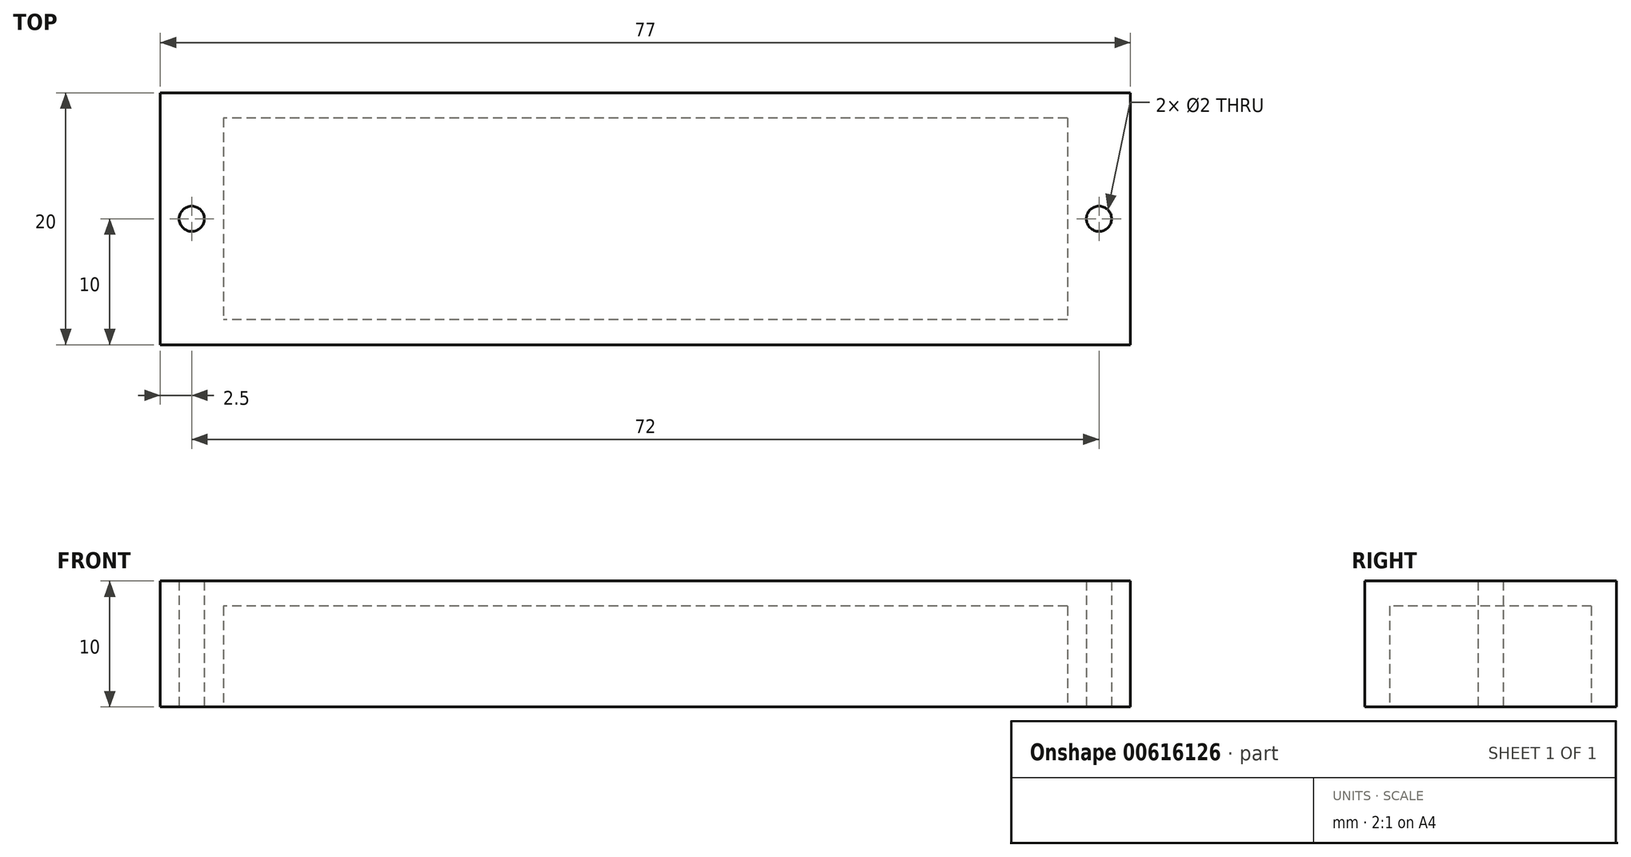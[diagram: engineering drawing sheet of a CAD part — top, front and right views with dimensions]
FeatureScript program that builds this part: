
annotation { "Feature Type Name" : "Feature", "Feature Type Description" : "" }
export const myFeature = defineFeature(function(context is Context, id is Id, definition is map)
    precondition{}
    {
        {
            var Q0;
            Q0=qCreatedBy(makeId("Top.planeOp"),FACE);
            var sketch = newSketch(context, id + "F0", { "sketchPlane" : qUnion([Q0])});
            skLineSegment(sketch, "E0.bottom", {"start": v(38.5, 10) * mm, "end": v(-38.5, 10) * mm});
            skLineSegment(sketch, "E0.top", {"start": v(38.5, -10) * mm, "end": v(-38.5, -10) * mm});
            skLineSegment(sketch, "E0.left", {"start": v(38.5, 10) * mm, "end": v(38.5, -10) * mm});
            skLineSegment(sketch, "E0.right", {"start": v(-38.5, 10) * mm, "end": v(-38.5, -10) * mm});
            skPoint(sketch, "E0.middle", {"position": v(0, 0) * mm});
            skPoint(sketch, "E1.left.start.orphan", {"position": v(33.5, 8) * mm});
            skPoint(sketch, "E1.top.start.orphan", {"position": v(33.5, -8) * mm});
            skPoint(sketch, "E1.right.end.orphan", {"position": v(-33.5, -8) * mm});
            skPoint(sketch, "E1.right.start.orphan", {"position": v(-33.5, 8) * mm});
            skSolve(sketch);
        }
        {
            var Q0;
            Q0 = qSketchRegion(id + "F0", true);
            extrude(context, id + "F1", {"entities" : qUnion([Q0]), "depth" : 10 * mm, "offsetDistance" : 25 * mm});
        }
        {
            var Q0;
            Q0=makeQuery(id+"F1.opExtrude","CAP_FACE",FACE,{"disambiguationData":[OSD([sQuery(id+"F0.wireOp",EDGE,"E0.bottom"),sQuery(id+"F0.wireOp",EDGE,"E0.top"),sQuery(id+"F0.wireOp",EDGE,"E0.left"),sQuery(id+"F0.wireOp",EDGE,"E0.right")])],"isStart":false});
            var sketch = newSketch(context, id + "F2", { "sketchPlane" : qUnion([Q0])});
            skLineSegment(sketch, "E2.bottom", {"start": v(33.5, 8) * mm, "end": v(-33.5, 8) * mm});
            skLineSegment(sketch, "E2.top", {"start": v(33.5, -8) * mm, "end": v(-33.5, -8) * mm});
            skLineSegment(sketch, "E2.left", {"start": v(33.5, 8) * mm, "end": v(33.5, -8) * mm});
            skLineSegment(sketch, "E2.right", {"start": v(-33.5, 8) * mm, "end": v(-33.5, -8) * mm});
            skPoint(sketch, "E2.middle", {"position": v(0, 0) * mm});
            skSolve(sketch);
        }
        {
            var Q0;
            Q0 = qSketchRegion(id + "F2", true);
            extrude(context, id + "F3", {"entities" : qUnion([Q0]), "operationType" : NewBodyOperationType.REMOVE, "oppositeDirection" : true, "depth" : 8 * mm, "offsetDistance" : 25 * mm});
        }
        {
            var Q0;
            Q0=qCreatedBy(makeId("Top.planeOp"),FACE);
            cPlane(context, id + "F4", {"entities" : qUnion([Q0]), "cplaneType" : CPlaneType.OFFSET, "offset" : 25 * mm, "width" : 150 * mm, "height" : 150 * mm});
        }
        {
            var Q0;
            Q0=makeQuery(id+"F1.opExtrude","SWEPT_BODY",BODY,{"disambiguationData":[OSD([sQuery(id+"F0.wireOp",EDGE,"E0.bottom"),sQuery(id+"F0.wireOp",EDGE,"E0.top"),sQuery(id+"F0.wireOp",EDGE,"E0.left"),sQuery(id+"F0.wireOp",EDGE,"E0.right")])]});
            var Q1;
            Q1=qCreatedBy(id+"F4.planeOp",FACE);
            mirror(context, id + "F5", {"entities" : qUnion([Q0]), "mirrorPlane" : qUnion([Q1])});
        }
        {
            var Q0;
            Q0=makeQuery(id+"F1.opExtrude","SWEPT_BODY",BODY,{"disambiguationData":[OSD([sQuery(id+"F0.wireOp",EDGE,"E0.bottom"),sQuery(id+"F0.wireOp",EDGE,"E0.top"),sQuery(id+"F0.wireOp",EDGE,"E0.left"),sQuery(id+"F0.wireOp",EDGE,"E0.right")])]});
            deleteBodies(context, id + "F6", {"entities" : qUnion([Q0])});
        }
        {
            var Q0;
            Q0=makeQuery(id+"F5.opPattern","COPY",FACE,{"derivedFrom":makeQuery(id+"F1.opExtrude","CAP_FACE",FACE,{"disambiguationData":[OSD([sQuery(id+"F0.wireOp",EDGE,"E0.bottom"),sQuery(id+"F0.wireOp",EDGE,"E0.top"),sQuery(id+"F0.wireOp",EDGE,"E0.left"),sQuery(id+"F0.wireOp",EDGE,"E0.right")])],"isStart":false}),"instanceName":"1"});
            var sketch = newSketch(context, id + "F7", { "sketchPlane" : qUnion([Q0])});
            skPoint(sketch, "E3", {"position": v(36, 0) * mm});
            skPoint(sketch, "E4", {"position": v(-36, 0) * mm});
            skCircle(sketch, "E5", {"center": v(36, 0) * mm, "radius": 1 * mm});
            skCircle(sketch, "E6", {"center": v(-36, 0) * mm, "radius": 1 * mm});
            skSolve(sketch);
        }
        {
            var Q0;
            Q0 = qSketchRegion(id + "F7", true);
            extrude(context, id + "F8", {"entities" : qUnion([Q0]), "operationType" : NewBodyOperationType.REMOVE, "oppositeDirection" : true, "depth" : 25 * mm, "offsetDistance" : 25 * mm});
        }
    });
